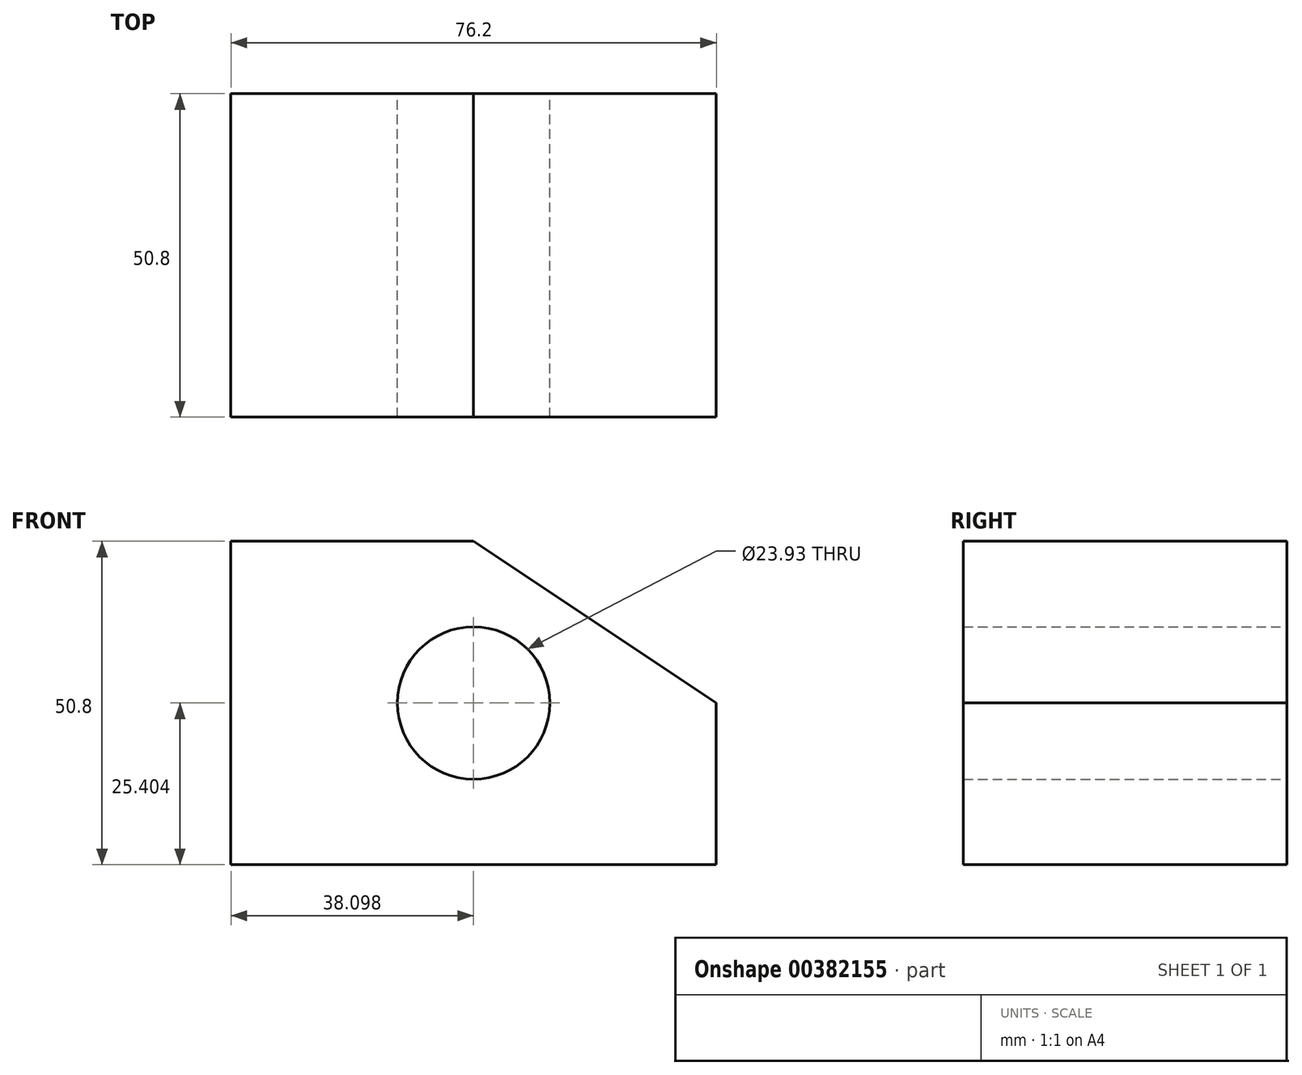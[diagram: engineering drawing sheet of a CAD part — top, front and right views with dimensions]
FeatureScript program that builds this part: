
annotation { "Feature Type Name" : "Feature", "Feature Type Description" : "" }
export const myFeature = defineFeature(function(context is Context, id is Id, definition is map)
    precondition{}
    {
        {
            var Q0;
            Q0=qCreatedBy(makeId("Front.planeOp"),FACE);
            var sketch = newSketch(context, id + "F0", { "sketchPlane" : qUnion([Q0])});
            skLineSegment(sketch, "E0", {"start": v(-55.8, 33.22) * mm, "end": v(-55.8, -17.58) * mm});
            skLineSegment(sketch, "E1", {"start": v(-55.8, -17.58) * mm, "end": v(20.4, -17.58) * mm});
            skLineSegment(sketch, "E2", {"start": v(20.4, -17.58) * mm, "end": v(20.4, 7.82) * mm});
            skLineSegment(sketch, "E3", {"start": v(-55.8, 33.22) * mm, "end": v(-17.7, 33.22) * mm});
            skLineSegment(sketch, "E4", {"start": v(-17.7, 33.22) * mm, "end": v(20.4, 7.82) * mm});
            skCircle(sketch, "E5", {"center": v(-17.7, 7.82) * mm, "radius": 11.96 * mm});
            skSolve(sketch);
        }
        {
            var Q0;
            Q0=makeQuery(id+"F0.imprint","IMPRINT",FACE,{"disambiguationData":[TD([[makeQuery(id+"F0.imprint","IMPRINT",EDGE,{"derivedFrom":sQuery(id+"F0.wireOp",EDGE,"E0")}),1.0]])]});
            extrude(context, id + "F1", {"entities" : qUnion([Q0]), "depth" : 50.8 * mm});
        }
    });
